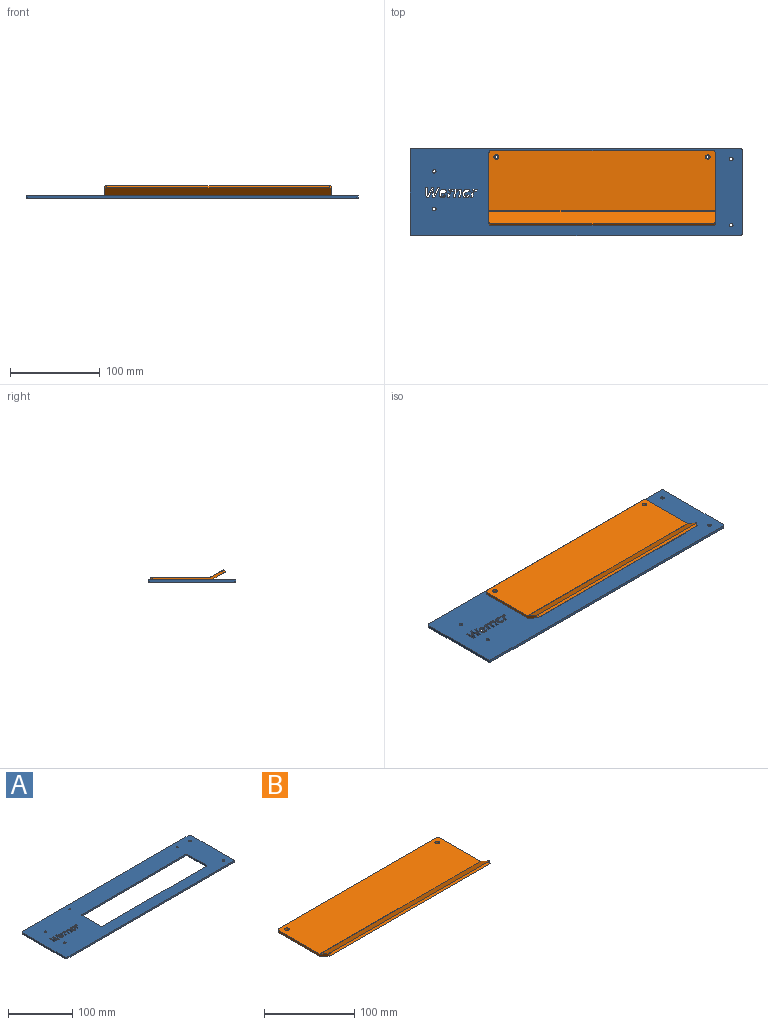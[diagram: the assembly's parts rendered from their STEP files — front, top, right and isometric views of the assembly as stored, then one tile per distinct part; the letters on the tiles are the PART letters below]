
ASSEMBLY  parts=2 mates=1
PART A: 137 faces, bbox 370x98x3 mm
  f0: extruded ~3x0.01mm, area 0mm2, adj f12,f116,f117,f125
  f1: plane 3.92x3mm, normal (0.98,-0.19,0), area 12mm2, adj f15,f116,f117,f126
  f2: extruded ~3x1.28mm, area 3.9mm2, adj f16,f116,f117,f125
  f3: extruded ~3x1.75mm, area 6mm2, adj f33,f116,f117,f123
  f4: extruded ~3x1.04mm, area 3.6mm2, adj f57,f116,f117,f120
  f5: extruded ~3x0.21mm, area 0.6mm2, adj f58,f116,f117,f122
  f6: plane 3.92x3mm, normal (0.98,-0.19,0), area 12mm2, adj f59,f116,f117,f121
  f7: extruded ~3x1.29mm, area 3.9mm2, adj f60,f116,f117,f119
  f8: extruded ~3x0.39mm, area 1.2mm2, adj f105,f116,f117,f118
  f9: extruded ~3x0.85mm, area 2.6mm2, adj f10,f115,f116,f117
  f10: plane 3x1.93mm, normal (-0.98,0.19,0), area 5.9mm2, adj f9,f11,f116,f117
  f11: extruded ~3x0.94mm, area 2.8mm2, adj f10,f12,f116,f117
  f12: extruded ~3x1.65mm, area 5.6mm2, adj f0,f11,f116,f117
  f13: extruded ~3x1.22mm, area 3.8mm2, adj f14,f116,f117,f127
  f14: plane 4.23x3mm, normal (-0.98,0.19,0), area 12.9mm2, adj f13,f15,f116,f117
  f15: plane 3x2.31mm, normal (0,1,0), area 6.9mm2, adj f1,f14,f116,f117
  f16: plane 3x2.2mm, normal (0,-1,0), area 6.6mm2, adj f2,f17,f116,f117
  f17: plane 3x1.41mm, normal (-0.99,0.13,0), area 4.3mm2, adj f16,f18,f116,f117
  f18: plane 3x0.4mm, normal (-0.99,0.16,0), area 1.2mm2, adj f17,f19,f116,f117
  f19: plane 3x0.03mm, normal (0,-1,0), area 0.1mm2, adj f18,f20,f116,f117
  f20: extruded ~3x1.54mm, area 5.9mm2, adj f19,f115,f116,f117
  f21: extruded ~3x0.73mm, area 2.2mm2, adj f22,f116,f117,f124
  f22: extruded ~3x1.34mm, area 4.3mm2, adj f21,f23,f116,f117
  f23: extruded ~3x1.13mm, area 3.8mm2, adj f22,f24,f116,f117
  f24: extruded ~3x1.75mm, area 7.2mm2, adj f23,f25,f116,f117
  f25: plane 3x2.01mm, normal (-0.29,-0.96,0), area 6.3mm2, adj f24,f26,f116,f117
  f26: extruded ~3x1.82mm, area 7.2mm2, adj f25,f27,f116,f117
  f27: extruded ~3x2.39mm, area 7.4mm2, adj f26,f28,f116,f117
  f28: extruded ~3x2.74mm, area 8.9mm2, adj f27,f29,f116,f117
  f29: extruded ~3x2.65mm, area 8.7mm2, adj f28,f30,f116,f117
  f30: extruded ~3x2.98mm, area 9.2mm2, adj f29,f31,f116,f117
  f31: extruded ~3x1.96mm, area 7.9mm2, adj f30,f32,f116,f117
  f32: extruded ~3x2.52mm, area 7.9mm2, adj f31,f33,f116,f117
  f33: extruded ~3x2.65mm, area 8.6mm2, adj f3,f32,f116,f117
  f34: plane 5.38x3mm, normal (-0.98,0.19,0), area 16.4mm2, adj f35,f103,f116,f117
  f35: plane 3x2.3mm, normal (0,1,0), area 6.9mm2, adj f34,f36,f116,f117
  f36: plane 4.9x3mm, normal (0.98,-0.19,0), area 15mm2, adj f35,f37,f116,f117
  f37: extruded ~3x1.36mm, area 4.1mm2, adj f36,f38,f116,f117
  f38: extruded ~3x1.25mm, area 5.6mm2, adj f37,f39,f116,f117
  f39: extruded ~3x1.54mm, area 5.2mm2, adj f38,f40,f116,f117
  f40: extruded ~3x1.65mm, area 5.7mm2, adj f39,f41,f116,f117
  f41: plane 4.99x3mm, normal (-0.98,0.19,0), area 15.2mm2, adj f40,f42,f116,f117
  f42: plane 3x2.32mm, normal (0,1,0), area 7mm2, adj f41,f43,f116,f117
  f43: plane 7x3mm, normal (0.98,-0.19,0), area 21.4mm2, adj f42,f44,f116,f117
  f44: extruded ~3x1.9mm, area 5.8mm2, adj f43,f45,f116,f117
  f45: plane 3x2.2mm, normal (0,-1,0), area 6.6mm2, adj f44,f46,f116,f117
  f46: extruded ~3x0.69mm, area 2.1mm2, adj f45,f47,f116,f117
  f47: extruded ~3x0.83mm, area 2.5mm2, adj f46,f48,f116,f117
  f48: plane 3x0.03mm, normal (0,-1,0), area 0.1mm2, adj f47,f49,f116,f117
  f49: extruded ~3x1.36mm, area 5.6mm2, adj f48,f50,f116,f117
  f50: extruded ~3x1.71mm, area 5.3mm2, adj f49,f51,f116,f117
  f51: extruded ~3x1.89mm, area 6.1mm2, adj f50,f52,f116,f117
  f52: extruded ~3x1.74mm, area 5.7mm2, adj f51,f53,f116,f117
  f53: extruded ~3x0.65mm, area 2mm2, adj f52,f103,f116,f117
  f54: extruded ~3x0.85mm, area 2.6mm2, adj f55,f104,f116,f117
  f55: plane 3x1.93mm, normal (-0.98,0.19,0), area 5.9mm2, adj f54,f56,f116,f117
  f56: extruded ~3x0.94mm, area 2.8mm2, adj f55,f57,f116,f117
  f57: extruded ~3x1.65mm, area 5.6mm2, adj f4,f56,f116,f117
  f58: plane 4.23x3mm, normal (-0.98,0.19,0), area 12.9mm2, adj f5,f59,f116,f117
  f59: plane 3x2.31mm, normal (0,1,0), area 6.9mm2, adj f6,f58,f116,f117
  f60: plane 3x2.2mm, normal (0,-1,0), area 6.6mm2, adj f7,f61,f116,f117
  f61: plane 3x1.41mm, normal (-0.99,0.13,0), area 4.3mm2, adj f60,f62,f116,f117
  f62: plane 3x0.4mm, normal (-0.99,0.16,0), area 1.2mm2, adj f61,f63,f116,f117
  f63: plane 3x0.03mm, normal (0,-1,0), area 0.1mm2, adj f62,f64,f116,f117
  f64: extruded ~3x1.54mm, area 5.9mm2, adj f63,f104,f116,f117
  f65: extruded ~3x0.73mm, area 2.2mm2, adj f66,f116,f117,f118
  f66: extruded ~3x1.34mm, area 4.3mm2, adj f65,f67,f116,f117
  f67: extruded ~3x1.13mm, area 3.8mm2, adj f66,f68,f116,f117
  f68: extruded ~3x1.75mm, area 7.2mm2, adj f67,f69,f116,f117
  f69: plane 3x2.01mm, normal (-0.29,-0.96,0), area 6.3mm2, adj f68,f70,f116,f117
  f70: extruded ~3x1.82mm, area 7.2mm2, adj f69,f71,f116,f117
  f71: extruded ~3x2.39mm, area 7.4mm2, adj f70,f72,f116,f117
  f72: extruded ~3x2.74mm, area 8.9mm2, adj f71,f73,f116,f117
  f73: extruded ~3x2.65mm, area 8.7mm2, adj f72,f74,f116,f117
  f74: extruded ~3x2.98mm, area 9.2mm2, adj f73,f75,f116,f117
  f75: extruded ~3x1.96mm, area 7.9mm2, adj f74,f76,f116,f117
  f76: extruded ~3x2.52mm, area 7.9mm2, adj f75,f77,f116,f117
  f77: extruded ~3x2.65mm, area 8.6mm2, adj f76,f105,f116,f117
  f78: plane 3x2.39mm, normal (0,-1,0), area 7.2mm2, adj f79,f106,f116,f117
  f79: plane 11.6x5.25mm, normal (-0.91,0.41,0), area 38.2mm2, adj f78,f80,f116,f117
  f80: plane 3x2.88mm, normal (0,1,0), area 8.6mm2, adj f79,f81,f116,f117
  f81: plane 6.68x3mm, normal (1,0.03,0), area 20.1mm2, adj f80,f82,f116,f117
  f82: plane 3x1.81mm, normal (1,0.02,0), area 5.4mm2, adj f81,f83,f116,f117
  f83: plane 3x0.69mm, normal (1,0.02,0), area 2.1mm2, adj f82,f84,f116,f117
  f84: extruded ~3x1.97mm, area 6.3mm2, adj f83,f85,f116,f117
  f85: extruded ~7.22x3.07mm, area 23.5mm2, adj f84,f86,f116,f117
  f86: plane 3x2.92mm, normal (0,1,0), area 8.8mm2, adj f85,f87,f116,f117
  f87: plane 11.6x3mm, normal (1,0.06,0), area 34.9mm2, adj f86,f88,f116,f117
  f88: plane 3x2.3mm, normal (0,-1,0), area 6.9mm2, adj f87,f89,f116,f117
  f89: plane 6.71x3mm, normal (-1,-0.04,0), area 20.1mm2, adj f88,f90,f116,f117
  f90: extruded ~3x2.85mm, area 8.5mm2, adj f89,f91,f116,f117
  f91: plane 3x1.19mm, normal (0.93,-0.37,0), area 3.8mm2, adj f90,f92,f116,f117
  f92: plane 3x1.52mm, normal (0.92,-0.38,0), area 4.9mm2, adj f91,f93,f116,f117
  f93: plane 6.85x3mm, normal (0.92,-0.39,0), area 22.3mm2, adj f92,f94,f116,f117
  f94: plane 3x2.6mm, normal (0,-1,0), area 7.8mm2, adj f93,f95,f116,f117
  f95: plane 9.55x3mm, normal (-1,-0.04,0), area 28.7mm2, adj f94,f96,f116,f117
  f96: extruded ~3x1.68mm, area 5.4mm2, adj f95,f106,f116,f117
  f97: plane 94x3mm, normal (-1,0,0), area 282mm2, adj f116,f117,f129,f132
  f98: plane 366x3mm, normal (0,-1,0), area 1098mm2, adj f116,f117,f129,f130
  f99: plane 94x3mm, normal (1,0,0), area 282mm2, adj f116,f117,f130,f131
  f100: plane 228x3mm, normal (0,1,0), area 684mm2, adj f116,f117,f133,f136
  f101: plane 41x3mm, normal (1,0,0), area 123mm2, adj f116,f117,f133,f134
  f102: plane 228x3mm, normal (0,-1,0), area 684mm2, adj f116,f117,f134,f135
  f103: extruded ~3x0.69mm, area 2.1mm2, adj f34,f53,f116,f117
  f104: extruded ~3x1.34mm, area 4.3mm2, adj f54,f64,f116,f117
  f105: extruded ~3x2.5mm, area 8.2mm2, adj f8,f77,f116,f117
  f106: extruded ~7.87x3.22mm, area 25.5mm2, adj f78,f96,f116,f117
  f107: plane 366x3mm, normal (0,1,0), area 1098mm2, adj f116,f117,f131,f132
  f108: plane 41x3mm, normal (-1,0,0), area 123mm2, adj f116,f117,f135,f136
  f109: cylinder r=2mm len=4mm, axis (0,0,-1), area 37.7mm2, adj f116,f117
  f110: cylinder r=2mm len=4mm, axis (0,0,-1), area 37.7mm2, adj f116,f117
  f111: cylinder r=2mm len=4mm, axis (0,0,-1), area 37.7mm2, adj f116,f117
  f112: cylinder r=2mm len=4mm, axis (0,0,-1), area 37.7mm2, adj f116,f117
  f113: cylinder r=1.5mm len=3mm, axis (0,0,-1), area 28.3mm2, adj f116,f117
  f114: cylinder r=1.5mm len=3mm, axis (0,0,-1), area 28.3mm2, adj f116,f117
  f115: extruded ~3x1.34mm, area 4.3mm2, adj f9,f20,f116,f117
  f116: plane 370x98mm, normal (0,0,1), area 25489.4mm2, adj f0,f1,f2,f3,f4,f5,f6,f7
  f117: plane 370x98mm, normal (0,0,-1), area 25489.4mm2, adj f0,f1,f2,f3,f4,f5,f6,f7
  f118: plane 5.95x3mm, normal (-0.23,0.97,0), area 18.3mm2, adj f8,f65,f116,f117
  f119: extruded ~3x2.24mm, area 9.8mm2, adj f7,f116,f117,f120
  f120: plane 3x0.32mm, normal (0,1,0), area 0.9mm2, adj f4,f116,f117,f119
  f121: plane 3x0.19mm, normal (0,-1,0), area 0.6mm2, adj f6,f116,f117,f122
  f122: plane 3x2.24mm, normal (0.23,-0.97,0), area 6.9mm2, adj f5,f116,f117,f121
  f123: extruded ~5.6x3mm, area 17.3mm2, adj f3,f116,f117,f124
  f124: plane 3x1.51mm, normal (-0.98,0.19,0), area 4.6mm2, adj f21,f116,f117,f123
  f125: extruded ~3x2.59mm, area 9.1mm2, adj f0,f2,f116,f117
  f126: plane 3x0.04mm, normal (0,-1,0), area 0.1mm2, adj f1,f116,f117,f128
  f127: plane 3x2.4mm, normal (0,-1,0), area 7.2mm2, adj f13,f116,f117,f128
  f128: plane 3x1.52mm, normal (0.98,-0.19,0), area 4.7mm2, adj f116,f117,f126,f127
  f129: cylinder r=2mm len=3mm, axis (0,0,-1), area 9.4mm2, adj f97,f98,f116,f117
  f130: cylinder r=2mm len=3mm, axis (0,0,1), area 9.4mm2, adj f98,f99,f116,f117
  f131: cylinder r=2mm len=3mm, axis (0,0,-1), area 9.4mm2, adj f99,f107,f116,f117
  f132: cylinder r=2mm len=3mm, axis (0,0,1), area 9.4mm2, adj f97,f107,f116,f117
  f133: cylinder r=2mm len=3mm, axis (0,0,1), area 9.4mm2, adj f100,f101,f116,f117
  f134: cylinder r=2mm len=3mm, axis (0,0,-1), area 9.4mm2, adj f101,f102,f116,f117
  f135: cylinder r=2mm len=3mm, axis (0,0,1), area 9.4mm2, adj f102,f108,f116,f117
  f136: cylinder r=2mm len=3mm, axis (0,0,-1), area 9.4mm2, adj f100,f108,f116,f117
PART B: 16 faces, bbox 252x83x11.3 mm
  f0: plane 79.27x10.26mm, normal (1,0,0), area 241.4mm2, adj f2,f3,f5,f7,f10,f11,f14,f15
  f1: plane 79.27x10.26mm, normal (-1,0,0), area 241.4mm2, adj f2,f3,f5,f7,f12,f13,f14,f15
  f2: plane 252x66.66mm, normal (0,0,-1), area 16757.4mm2, adj f0,f1,f4,f8,f9,f10,f13,f14
  f3: plane 252x13.84mm, normal (0,-0.5,-0.87), area 4025.4mm2, adj f0,f1,f6,f11,f12,f14
  f4: plane 248x3mm, normal (0,1,0), area 744mm2, adj f2,f5,f10,f13
  f5: plane 252x66.66mm, normal (0,0,1), area 16757.4mm2, adj f0,f1,f4,f8,f9,f10,f13,f15
  f6: plane 248x2.6mm, normal (0,-0.87,0.5), area 744mm2, adj f3,f7,f11,f12
  f7: plane 252x13.84mm, normal (0,0.5,0.87), area 4025.4mm2, adj f0,f1,f6,f11,f12,f15
  f8: cylinder r=2.5mm len=5mm, axis (0,0,1), area 47.1mm2, adj f2,f5
  f9: cylinder r=2.5mm len=5mm, axis (0,0,1), area 47.1mm2, adj f2,f5
  f10: cylinder r=2mm len=3mm, axis (0,0,-1), area 9.4mm2, adj f0,f2,f4,f5
  f11: cylinder r=2mm len=3.6mm, axis (0,0.5,0.87), area 9.4mm2, adj f0,f3,f6,f7
  f12: cylinder r=2mm len=3.6mm, axis (0,-0.5,-0.87), area 9.4mm2, adj f1,f3,f6,f7
  f13: cylinder r=2mm len=3mm, axis (0,0,1), area 9.4mm2, adj f1,f2,f4,f5
  f14: cylinder r=5mm len=252mm, axis (-1,0,0), area 659.7mm2, adj f0,f1,f2,f3
  f15: cylinder r=2mm len=252mm, axis (1,0,0), area 263.9mm2, adj f0,f1,f5,f7
PLACE A t=(0,94,-3)mm
PLACE B at identity
MATE fastened A.f113 <-> B.f9  axis (0,0,1) through (-89,133,0)mm
